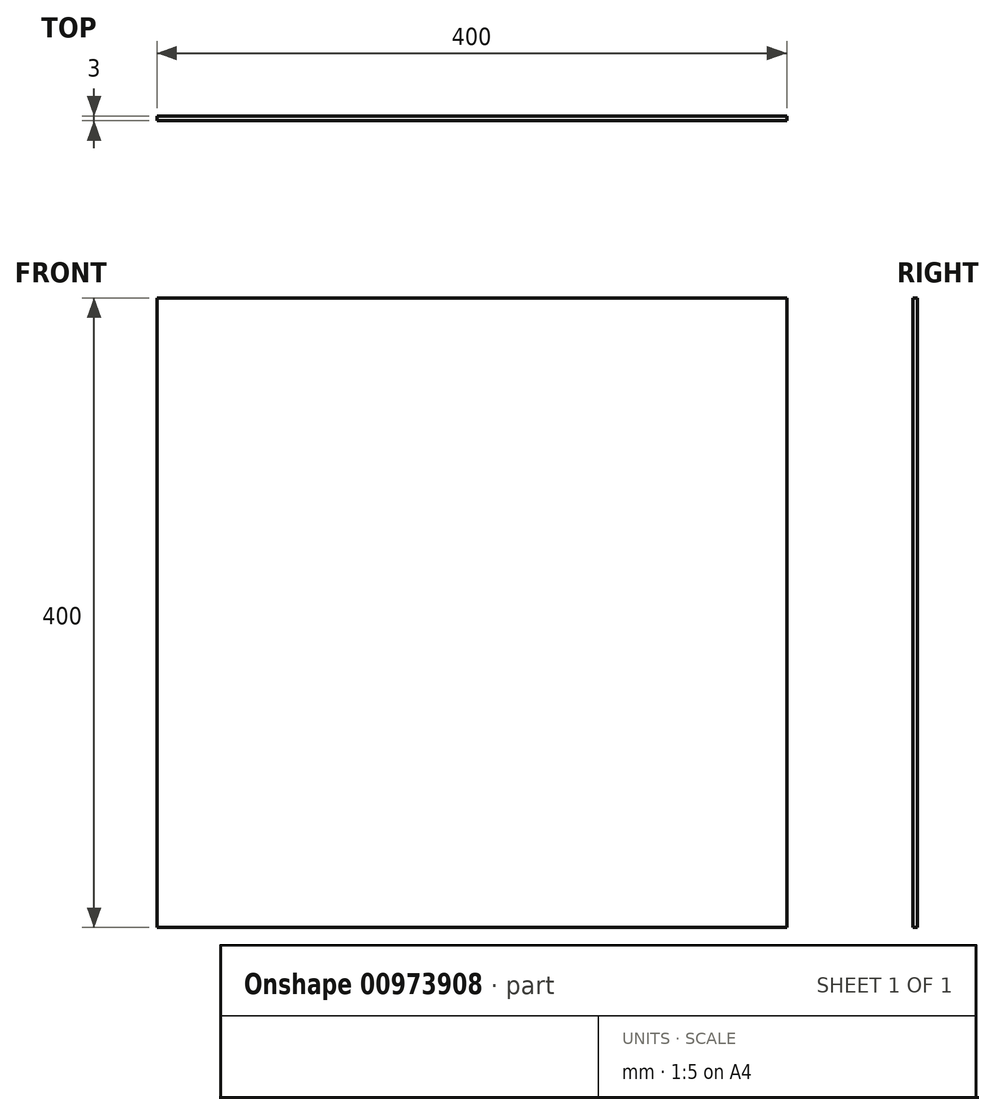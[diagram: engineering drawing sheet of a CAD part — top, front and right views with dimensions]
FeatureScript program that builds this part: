
annotation { "Feature Type Name" : "Feature", "Feature Type Description" : "" }
export const myFeature = defineFeature(function(context is Context, id is Id, definition is map)
    precondition{}
    {
        {
            var Q0;
            Q0=qCreatedBy(makeId("Front.planeOp"),FACE);
            var sketch = newSketch(context, id + "F0", { "sketchPlane" : qUnion([Q0])});
            skLineSegment(sketch, "E0.bottom", {"start": v(-200, 200) * mm, "end": v(200, 200) * mm});
            skLineSegment(sketch, "E0.top", {"start": v(-200, -200) * mm, "end": v(200, -200) * mm});
            skLineSegment(sketch, "E0.left", {"start": v(-200, 200) * mm, "end": v(-200, -200) * mm});
            skLineSegment(sketch, "E0.right", {"start": v(200, 200) * mm, "end": v(200, -200) * mm});
            skPoint(sketch, "E0.middle", {"position": v(0, 0) * mm});
            skSolve(sketch);
        }
        {
            var Q0;
            Q0 = qSketchRegion(id + "F0", true);
            extrude(context, id + "F1", {"entities" : qUnion([Q0]), "depth" : 3 * mm, "offsetDistance" : 25 * mm});
        }
    });
